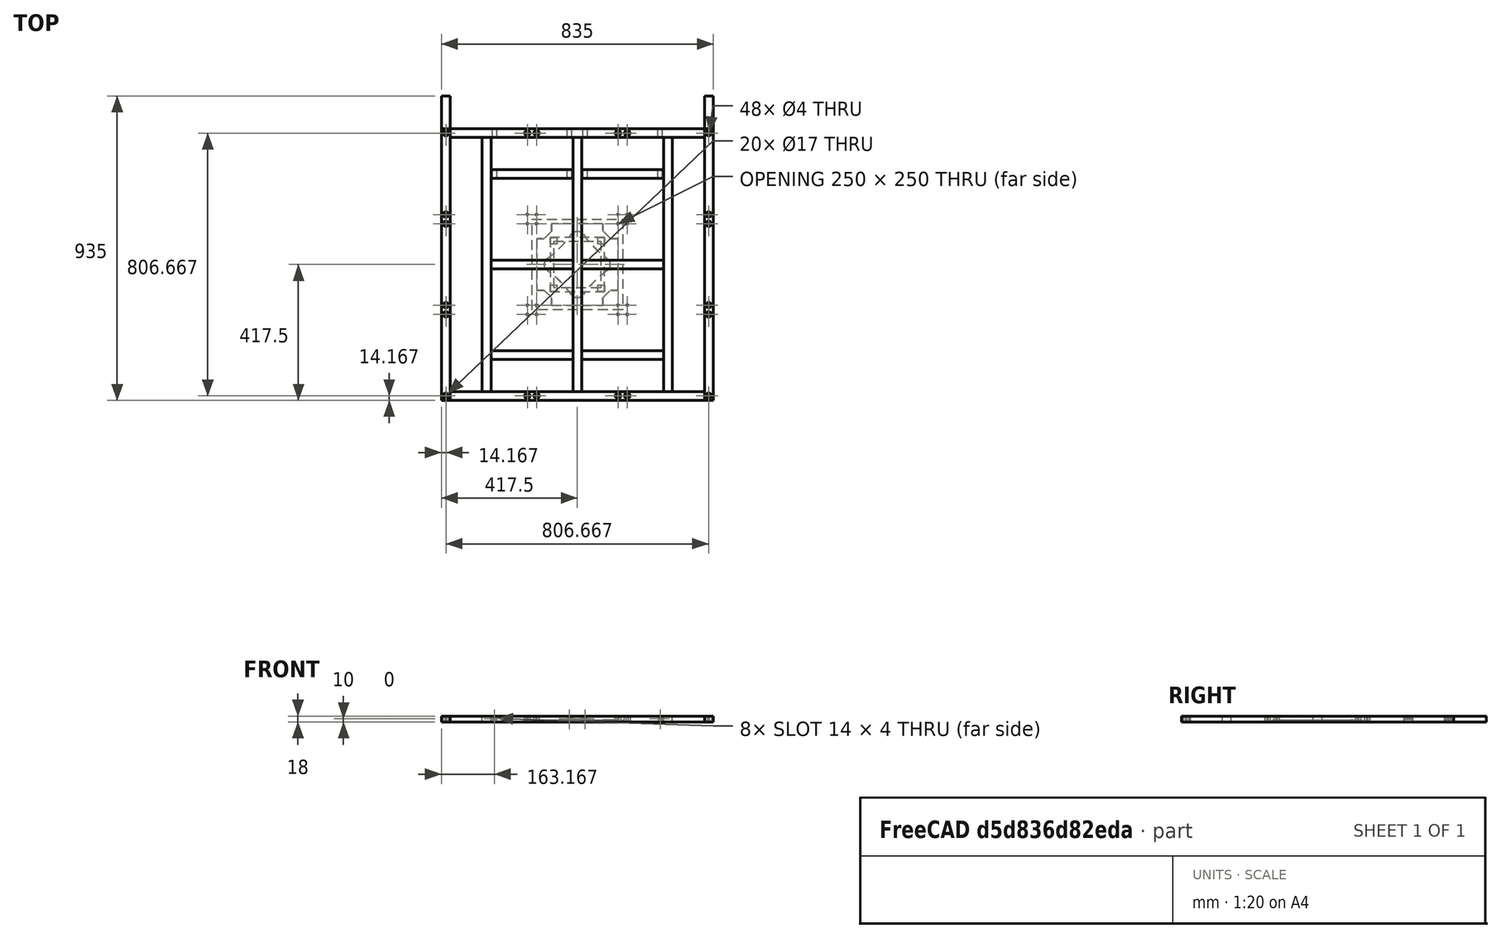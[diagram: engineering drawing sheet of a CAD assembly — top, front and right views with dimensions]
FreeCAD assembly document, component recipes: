
FREECAD ASSEMBLY — COMPONENT RECIPES ("DancePad")

This assembly document has 11 components, labeled P0..P10 below (a component is one placed body or linked part). 11 of them carry a construction recipe — the FreeCAD feature program that regenerates the part from scratch, quoted from this document or its linked companion documents; the rest are supplied as boundary geometry only. No exploded tour is included for this assembly.
COMPONENT P0 — recipe-attached ("Pad_UpLeft_Part - Link(Pad_Up_Part)", modeled in this document).
Construction recipe (the document's own serialized feature program — sketch geometry with constraints, then the solid features built on it; lengths are millimeters unless a unit is written):

FEATURE [Sketcher::SketchObject] Sketch002
  ArcFitTolerance = 0
  AttachmentSupport = -> [XY_Plane002]
  ExternalTypes = [0]
  FullyConstrained = true
  MakeInternals = false
  MapMode = 5
  _ExternalGeoVersion = 0
  expr: Constraints[10] = <<Variables>>.PadLength
  expr: Constraints[9] = <<Variables>>.PadLength
  sketch-geometry (4):
    g0: LineSegment StartX=-139 StartY=139 StartZ=0 EndX=139 EndY=139 EndZ=0
    g1: LineSegment StartX=139 StartY=139 StartZ=0 EndX=139 EndY=-139 EndZ=0
    g2: LineSegment StartX=139 StartY=-139 StartZ=0 EndX=-139 EndY=-139 EndZ=0
    g3: LineSegment StartX=-139 StartY=-139 StartZ=0 EndX=-139 EndY=139 EndZ=0
  constraints (11):
    c: Coincident(g0,g1)
    c: Coincident(g1,g2)
    c: Coincident(g2,g3)
    c: Coincident(g3,g0)
    c: Horizontal(g0)
    c: Horizontal(g2)
    c: Vertical(g1)
    c: Vertical(g3)
    c: Symmetric(g0,g1,g-1)
    c: DistanceX(g0,g0) = 278
    c: DistanceY(g1,g1) = 278
FEATURE [PartDesign::Pad] Pad002
  Direction = (0,0,1)
  Length = 6
  Length2 = 100
  Profile = -> Sketch002
  SideType = 0
  Suppressed = false
  Type = 0
  Type2 = 0
  expr: Length = <<Variables>>.PadThickness
FEATURE [Sketcher::SketchObject] Sketch003
  ArcFitTolerance = 0
  AttachmentSupport = -> [XY_Plane002]
  ExternalTypes = [0]
  FullyConstrained = true
  MakeInternals = false
  MapMode = 5
  _ExternalGeoVersion = 0
  expr: Constraints[22] = <<Variables>>.PadLength - 120
  expr: Constraints[24] = <<Variables>>.PadLength - 120
  expr: Constraints[28] = <<Variables>>.PadLength / 2 - 14
  expr: Constraints[29] = <<Variables>>.PadLength / 2 - 14
  sketch-geometry (16):
    g0: LineSegment StartX=-79 StartY=125 StartZ=0 EndX=79 EndY=125 EndZ=0
    g1: LineSegment StartX=79 StartY=125 StartZ=0 EndX=79 EndY=102 EndZ=0
    g2: LineSegment StartX=79 StartY=102 StartZ=0 EndX=102 EndY=79 EndZ=0
    g3: LineSegment StartX=102 StartY=79 StartZ=0 EndX=125 EndY=79 EndZ=0
    g4: LineSegment StartX=125 StartY=79 StartZ=0 EndX=125 EndY=-79 EndZ=0
    g5: LineSegment StartX=125 StartY=-79 StartZ=0 EndX=102 EndY=-79 EndZ=0
    g6: LineSegment StartX=102 StartY=-79 StartZ=0 EndX=79 EndY=-102 EndZ=0
    g7: LineSegment StartX=79 StartY=-102 StartZ=0 EndX=79 EndY=-125 EndZ=0
    g8: LineSegment StartX=79 StartY=-125 StartZ=0 EndX=-79 EndY=-125 EndZ=0
    g9: LineSegment StartX=-79 StartY=-125 StartZ=0 EndX=-79 EndY=-102 EndZ=0
    g10: LineSegment StartX=-79 StartY=-102 StartZ=0 EndX=-102 EndY=-79 EndZ=0
    g11: LineSegment StartX=-102 StartY=-79 StartZ=0 EndX=-125 EndY=-79 EndZ=0
    g12: LineSegment StartX=-125 StartY=-79 StartZ=0 EndX=-125 EndY=79 EndZ=0
    g13: LineSegment StartX=-125 StartY=79 StartZ=0 EndX=-102 EndY=79 EndZ=0
    g14: LineSegment StartX=-102 StartY=79 StartZ=0 EndX=-79 EndY=102 EndZ=0
    g15: LineSegment StartX=-79 StartY=102 StartZ=0 EndX=-79 EndY=125 EndZ=0
  constraints (38):
    c: Coincident(g0,g1)
    c: Vertical(g1)
    c: Coincident(g1,g2)
    c: Coincident(g2,g3)
    c: Horizontal(g3)
    c: Coincident(g3,g4)
    c: Vertical(g4)
    c: Coincident(g4,g5)
    c: Horizontal(g5)
    c: Coincident(g5,g6)
    c: Coincident(g6,g7)
    c: Vertical(g7)
    c: Coincident(g7,g8)
    c: Horizontal(g8)
    c: Coincident(g8,g9)
    c: Coincident(g9,g10)
    c: Coincident(g10,g11)
    c: Coincident(g11,g12)
    c: Coincident(g12,g13)
    c: Coincident(g13,g14)
    c: Coincident(g14,g15)
    c: Coincident(g15,g0)
    c: DistanceX(g0,g0) = 158
    c: Symmetric(g0,g0,g-2)
    c: DistanceY(g12,g12) = 158
    c: Symmetric(g12,g11,g-1)
    c: DistanceY(g15,g15) = 23
    c: DistanceX(g13,g13) = 23
    c: DistanceY(g-1,g0) = 125
    c: DistanceX(g12,g-1) = 125
    c: Symmetric(g14,g1,g-2)
    c: Symmetric(g13,g2,g-2)
    c: Symmetric(g12,g3,g-2)
    c: Symmetric(g13,g10,g-1)
    c: Symmetric(g14,g9,g-1)
    c: Symmetric(g0,g8,g-1)
    c: Symmetric(g13,g5,g-1)
    c: Symmetric(g14,g6,g-1)
FEATURE [PartDesign::Pocket] Pocket
  BaseFeature = -> Pad002
  Direction = (0,0,-1)
  Length = 5
  Length2 = 100
  Profile = -> Sketch003
  SideType = 2
  Suppressed = false
  Type = 1
  Type2 = 0
FEATURE [Sketcher::SketchObject] Sketch004  label="Sketch_Screw_Holes"
  ArcFitTolerance = 0
  AttachmentSupport = -> [Pad002]
  ExternalTypes = [0]
  FullyConstrained = true
  MakeInternals = false
  MapMode = 5
  Placement = pos=(0,0,0) rot=(1,0,0;3.14159rad)
  _ExternalGeoVersion = 0
  expr: Constraints[0] = <<Variables>>.PadScrewDiameter
  expr: Constraints[1] = <<Variables>>.PadScrewDiameter
  expr: Constraints[2] = <<Variables>>.PadScrewDiameter
  expr: Constraints[3] = <<Variables>>.PadScrewDiameter
  expr: Constraints[4] = <<Variables>>.PadLength / 2 - <<Variables>>.ScrewCornerPosition
  expr: Constraints[5] = <<Variables>>.PadLength / 2 - <<Variables>>.ScrewCornerPosition
  sketch-geometry (4):
    g0: Circle CenterX=-125 CenterY=125 CenterZ=0 NormalX=0 NormalY=0 NormalZ=1 AngleXU=0 Radius=2
    g1: Circle CenterX=125 CenterY=125 CenterZ=0 NormalX=0 NormalY=0 NormalZ=1 AngleXU=0 Radius=2
    g2: Circle CenterX=125 CenterY=-125 CenterZ=0 NormalX=0 NormalY=0 NormalZ=1 AngleXU=0 Radius=2
    g3: Circle CenterX=-125 CenterY=-125 CenterZ=0 NormalX=0 NormalY=0 NormalZ=1 AngleXU=0 Radius=2
  constraints (9):
    c: Diameter(g0) = 4
    c: Diameter(g1) = 4
    c: Diameter(g2) = 4
    c: Diameter(g3) = 4
    c: DistanceX(g0,g-1) = 125
    c: DistanceY(g-1,g0) = 125
    c: Symmetric(g0,g1,g-2)
    c: Symmetric(g0,g3,g-1)
    c: Symmetric(g0,g2,g-1)
FEATURE [PartDesign::Pocket] Pocket001  label="Screw_Pocket"
  BaseFeature = -> Pocket
  Direction = (0,0,1)
  Length = 5
  Length2 = 100
  Profile = -> Sketch004
  SideType = 2
  Suppressed = false
  Type = 1
  Type2 = 0
FEATURE [PartDesign::Fillet] Fillet
  Base = -> Pocket001 [Edge48,Edge40,Edge39,Edge47]
  BaseFeature = -> Pocket001
  Radius = 3
  SupportTransform = false
  Suppressed = false
  UseAllEdges = false
FEATURE [PartDesign::Body] Body002  label="Border_Body"
  AllowCompound = true
  Group = -> [Sketch002,Pad002,Sketch003,Sketch004,Pocket,Pocket001,Fillet]
  Origin = -> Origin008
  Tip = -> Fillet
COMPONENT P1 — same part as P0; its construction recipe is shown at P0.
COMPONENT P2 — same part as P0; its construction recipe is shown at P0.
COMPONENT P3 — same part as P0; its construction recipe is shown at P0.
COMPONENT P4 — same part as P0; its construction recipe is shown at P0.
COMPONENT P5 — same part as P0; its construction recipe is shown at P0.
COMPONENT P6 — same part as P0; its construction recipe is shown at P0.
COMPONENT P7 — recipe-attached ("PolycarbonatePad_Part", modeled in this document).
Construction recipe (the document's own serialized feature program — sketch geometry with constraints, then the solid features built on it; lengths are millimeters unless a unit is written):

FEATURE [Sketcher::SketchObject] Sketch022
  ArcFitTolerance = 0
  AttachmentSupport = -> [XY_Plane016]
  ExternalTypes = [0]
  FullyConstrained = true
  MakeInternals = false
  MapMode = 5
  _ExternalGeoVersion = 0
  expr: Constraints[8] = <<Variables>>.PadLength
  expr: Constraints[9] = <<Variables>>.PadLength
  sketch-geometry (4):
    g0: LineSegment StartX=-139 StartY=139 StartZ=0 EndX=139 EndY=139 EndZ=0
    g1: LineSegment StartX=139 StartY=139 StartZ=0 EndX=139 EndY=-139 EndZ=0
    g2: LineSegment StartX=139 StartY=-139 StartZ=0 EndX=-139 EndY=-139 EndZ=0
    g3: LineSegment StartX=-139 StartY=-139 StartZ=0 EndX=-139 EndY=139 EndZ=0
  constraints (11):
    c: Coincident(g0,g1)
    c: Coincident(g1,g2)
    c: Coincident(g2,g3)
    c: Coincident(g3,g0)
    c: Horizontal(g0)
    c: Horizontal(g2)
    c: Vertical(g1)
    c: Vertical(g3)
    c: DistanceX(g0,g0) = 278
    c: DistanceY(g1,g1) = 278
    c: Symmetric(g0,g1,g-1)
FEATURE [PartDesign::Pad] Pad015
  AlongSketchNormal = false
  Direction = (0,0,1)
  Length = 3
  Length2 = 100
  Profile = -> Sketch022
  SideType = 0
  Suppressed = false
  Type = 0
  Type2 = 0
  expr: Length = <<Variables>>.PolycarbonateThickness
FEATURE [Sketcher::SketchObject] Sketch023
  ArcFitTolerance = 0
  AttachmentSupport = -> [Pad015]
  ExternalTypes = [0]
  FullyConstrained = true
  MakeInternals = false
  MapMode = 5
  Placement = pos=(0,0,3) rot=(0,0,1;0rad)
  _ExternalGeoVersion = 0
  expr: Constraints[0] = <<Variables>>.PadScrewDiameter
  expr: Constraints[1] = <<Variables>>.PadScrewDiameter
  expr: Constraints[2] = <<Variables>>.PadScrewDiameter
  expr: Constraints[3] = <<Variables>>.PadScrewDiameter
  expr: Constraints[4] = <<Variables>>.PadLength / 2 - <<Variables>>.ScrewCornerPosition
  expr: Constraints[5] = <<Variables>>.PadLength / 2 - <<Variables>>.ScrewCornerPosition
  sketch-geometry (4):
    g0: Circle CenterX=-125 CenterY=125 CenterZ=0 NormalX=0 NormalY=0 NormalZ=1 AngleXU=0 Radius=2
    g1: Circle CenterX=125 CenterY=125 CenterZ=0 NormalX=0 NormalY=0 NormalZ=1 AngleXU=0 Radius=2
    g2: Circle CenterX=-125 CenterY=-125 CenterZ=0 NormalX=0 NormalY=0 NormalZ=1 AngleXU=0 Radius=2
    g3: Circle CenterX=125 CenterY=-125 CenterZ=0 NormalX=0 NormalY=0 NormalZ=1 AngleXU=0 Radius=2
  constraints (9):
    c: Diameter(g0) = 4
    c: Diameter(g1) = 4
    c: Diameter(g2) = 4
    c: Diameter(g3) = 4
    c: DistanceX(g0,g-1) = 125
    c: DistanceY(g-1,g0) = 125
    c: Symmetric(g0,g1,g-2)
    c: Symmetric(g0,g2,g-1)
    c: Symmetric(g0,g3,g-1)
FEATURE [PartDesign::Pocket] Pocket012
  BaseFeature = -> Pad015
  Direction = (0,0,-1)
  Length = 5
  Length2 = 100
  Profile = -> Sketch023
  SideType = 2
  Suppressed = false
  Type = 1
  Type2 = 0
FEATURE [PartDesign::Body] Body015
  AllowCompound = true
  Group = -> [Sketch022,Pad015,Sketch023,Pocket012]
  Origin = -> Origin027
  Tip = -> Pocket012
COMPONENT P8 — recipe-attached ("Body_Part", modeled in this document).
Construction recipe (the document's own serialized feature program — sketch geometry with constraints, then the solid features built on it; lengths are millimeters unless a unit is written):

FEATURE [Sketcher::SketchObject] Sketch
  ArcFitTolerance = 0
  AttachmentSupport = -> [XY_Plane]
  ExternalTypes = [0]
  FullyConstrained = true
  MakeInternals = false
  MapMode = 5
  _ExternalGeoVersion = 0
  expr: Constraints[10] = <<Variables>>.OveralPadLength
  expr: Constraints[9] = <<Variables>>.OveralPadLength
  sketch-geometry (4):
    g0: LineSegment StartX=-417.5 StartY=417.5 StartZ=0 EndX=417.5 EndY=417.5 EndZ=0
    g1: LineSegment StartX=417.5 StartY=417.5 StartZ=0 EndX=417.5 EndY=-417.5 EndZ=0
    g2: LineSegment StartX=417.5 StartY=-417.5 StartZ=0 EndX=-417.5 EndY=-417.5 EndZ=0
    g3: LineSegment StartX=-417.5 StartY=-417.5 StartZ=0 EndX=-417.5 EndY=417.5 EndZ=0
  constraints (11):
    c: Coincident(g0,g1)
    c: Coincident(g1,g2)
    c: Coincident(g2,g3)
    c: Coincident(g3,g0)
    c: Horizontal(g0)
    c: Horizontal(g2)
    c: Vertical(g1)
    c: Vertical(g3)
    c: Symmetric(g0,g1,g-1)
    c: DistanceX(g0,g0) = 835
    c: DistanceY(g1,g1) = 835
FEATURE [PartDesign::Pad] Pad
  Direction = (0,0,1)
  Length = 18
  Length2 = 100
  Profile = -> Sketch
  SideType = 0
  Suppressed = false
  Type = 0
  Type2 = 0
  expr: Length = <<Variables>>.OverallPadThickness
FEATURE [PartDesign::SubShapeBinder] Binder  label="Binder(Sketch_Screw_Holes)"
  BindCopyOnChange = 0
  BindMode = 0
  ClaimChildren = false
  Context = -> Part001 [Body.Binder.]
  Fuse = false
  MakeFace = true
  OffsetFill = false
  OffsetIntersection = false
  OffsetJoinType = 0
  OffsetOpenResult = false
  PartialLoad = false
  Relative = true
  Support = -> [Part002[Body002.Sketch004.]]
  _Version = 8
FEATURE [PartDesign::SubShapeBinder] Binder001  label="Binder001(Sketch_Screw_Holes)"
  BindCopyOnChange = 0
  BindMode = 0
  ClaimChildren = false
  Context = -> Part001 [Body.Binder001.]
  Fuse = false
  MakeFace = true
  OffsetFill = false
  OffsetIntersection = false
  OffsetJoinType = 0
  OffsetOpenResult = false
  PartialLoad = false
  Relative = true
  Support = -> [Link[Body002.Sketch004.]]
  _Version = 8
FEATURE [PartDesign::SubShapeBinder] Binder002  label="Binder002(Sketch_Screw_Holes)"
  BindCopyOnChange = 0
  BindMode = 0
  ClaimChildren = false
  Context = -> Part001 [Body.Binder002.]
  Fuse = false
  MakeFace = true
  OffsetFill = false
  OffsetIntersection = false
  OffsetJoinType = 0
  OffsetOpenResult = false
  PartialLoad = false
  Relative = true
  Support = -> [Link015[Body002.Sketch004.]]
  _Version = 8
FEATURE [PartDesign::SubShapeBinder] Binder003  label="Binder003(Sketch_Screw_Holes)"
  BindCopyOnChange = 0
  BindMode = 0
  ClaimChildren = false
  Context = -> Part001 [Body.Binder003.]
  Fuse = false
  MakeFace = true
  OffsetFill = false
  OffsetIntersection = false
  OffsetJoinType = 0
  OffsetOpenResult = false
  PartialLoad = false
  Relative = true
  Support = -> [Link016[Body002.Sketch004.]]
  _Version = 8
FEATURE [PartDesign::SubShapeBinder] Binder004  label="Binder004(Sketch_Screw_Holes)"
  BindCopyOnChange = 0
  BindMode = 0
  ClaimChildren = false
  Context = -> Part001 [Body.Binder004.]
  Fuse = false
  MakeFace = true
  OffsetFill = false
  OffsetIntersection = false
  OffsetJoinType = 0
  OffsetOpenResult = false
  PartialLoad = false
  Relative = true
  Support = -> [Link017[Body002.Sketch004.]]
  _Version = 8
FEATURE [PartDesign::SubShapeBinder] Binder005  label="Binder005(Sketch_Screw_Holes)"
  BindCopyOnChange = 0
  BindMode = 0
  ClaimChildren = false
  Context = -> Part001 [Body.Binder005.]
  Fuse = false
  MakeFace = true
  OffsetFill = false
  OffsetIntersection = false
  OffsetJoinType = 0
  OffsetOpenResult = false
  PartialLoad = false
  Relative = true
  Support = -> [Link018[Body002.Sketch004.]]
  _Version = 8
FEATURE [PartDesign::SubShapeBinder] Binder006  label="Binder006(Sketch_Screw_Holes)"
  BindCopyOnChange = 0
  BindMode = 0
  ClaimChildren = false
  Context = -> Part001 [Body.Binder006.]
  Fuse = false
  MakeFace = true
  OffsetFill = false
  OffsetIntersection = false
  OffsetJoinType = 0
  OffsetOpenResult = false
  PartialLoad = false
  Relative = true
  Support = -> [Link019[Body002.Sketch004.]]
  _Version = 8
FEATURE [PartDesign::SubShapeBinder] Binder007  label="Binder007(Sketch_Screw_Holes)"
  BindCopyOnChange = 0
  BindMode = 0
  ClaimChildren = false
  Context = -> Part001 [Body.Binder007.]
  Fuse = false
  MakeFace = true
  OffsetFill = false
  OffsetIntersection = false
  OffsetJoinType = 0
  OffsetOpenResult = false
  PartialLoad = false
  Relative = true
  Support = -> [Link020[Body002.Sketch004.]]
  _Version = 8
FEATURE [PartDesign::SubShapeBinder] Binder008  label="Binder008(Sketch021)"
  BindCopyOnChange = 0
  BindMode = 0
  ClaimChildren = false
  Context = -> Part001 [Body.Binder008.]
  Fuse = false
  MakeFace = true
  OffsetFill = false
  OffsetIntersection = false
  OffsetJoinType = 0
  OffsetOpenResult = false
  PartialLoad = false
  Relative = true
  Support = -> [Part007[Body014.Sketch021.]]
  _Version = 8
FEATURE [Sketcher::SketchObject] Sketch028
  ArcFitTolerance = 0
  AttachmentSupport = -> [Pad]
  ExternalGeometry = -> [Binder001,Binder,Binder002,Binder003,Binder008,Binder004,Binder005,Binder007,Binder006]
  ExternalTypes = [0]
  FullyConstrained = true
  MakeInternals = false
  MapMode = 5
  Placement = pos=(0,0,18) rot=(0,0,1;0rad)
  _ExternalGeoVersion = 0
  expr: Constraints[36] = <<Variables>>.PadScrewDiameter
  expr: Constraints[37] = <<Variables>>.PadScrewDiameter
  expr: Constraints[38] = <<Variables>>.PadScrewDiameter
  expr: Constraints[39] = <<Variables>>.PadScrewDiameter
  expr: Constraints[40] = <<Variables>>.PadScrewDiameter
  expr: Constraints[41] = <<Variables>>.PadScrewDiameter
  expr: Constraints[42] = <<Variables>>.PadScrewDiameter
  expr: Constraints[43] = <<Variables>>.PadScrewDiameter
  expr: Constraints[44] = <<Variables>>.PadScrewDiameter
  expr: Constraints[45] = <<Variables>>.PadScrewDiameter
  expr: Constraints[46] = <<Variables>>.PadScrewDiameter
  expr: Constraints[47] = <<Variables>>.PadScrewDiameter
  expr: Constraints[48] = <<Variables>>.PadScrewDiameter
  expr: Constraints[49] = <<Variables>>.PadScrewDiameter
  expr: Constraints[50] = <<Variables>>.PadScrewDiameter
  expr: Constraints[51] = <<Variables>>.PadScrewDiameter
  expr: Constraints[52] = <<Variables>>.PadScrewDiameter
  expr: Constraints[53] = <<Variables>>.PadScrewDiameter
  expr: Constraints[54] = <<Variables>>.PadScrewDiameter
  expr: Constraints[55] = <<Variables>>.PadScrewDiameter
  expr: Constraints[56] = <<Variables>>.PadScrewDiameter
  expr: Constraints[57] = <<Variables>>.PadScrewDiameter
  expr: Constraints[58] = <<Variables>>.PadScrewDiameter
  expr: Constraints[59] = <<Variables>>.PadScrewDiameter
  expr: Constraints[60] = <<Variables>>.PadScrewDiameter
  expr: Constraints[61] = <<Variables>>.PadScrewDiameter
  expr: Constraints[62] = <<Variables>>.PadScrewDiameter
  expr: Constraints[63] = <<Variables>>.PadScrewDiameter
  expr: Constraints[64] = <<Variables>>.PadScrewDiameter
  expr: Constraints[65] = <<Variables>>.PadScrewDiameter
  expr: Constraints[66] = <<Variables>>.PadScrewDiameter
  expr: Constraints[67] = <<Variables>>.PadScrewDiameter
  expr: Constraints[68] = <<Variables>>.PadScrewDiameter
  expr: Constraints[69] = <<Variables>>.PadScrewDiameter
  expr: Constraints[70] = <<Variables>>.PadScrewDiameter
  expr: Constraints[71] = <<Variables>>.PadScrewDiameter
  sketch-geometry (36):
    g0: Circle CenterX=-403.333 CenterY=403.333 CenterZ=0 NormalX=0 NormalY=0 NormalZ=1 AngleXU=0 Radius=2
    g1: Circle CenterX=-153.333 CenterY=403.333 CenterZ=0 NormalX=0 NormalY=0 NormalZ=1 AngleXU=0 Radius=2
    g2: Circle CenterX=-125 CenterY=403.333 CenterZ=0 NormalX=0 NormalY=0 NormalZ=1 AngleXU=0 Radius=2
    g3: Circle CenterX=125 CenterY=403.333 CenterZ=0 NormalX=0 NormalY=0 NormalZ=1 AngleXU=0 Radius=2
    g4: Circle CenterX=153.333 CenterY=403.333 CenterZ=0 NormalX=0 NormalY=0 NormalZ=1 AngleXU=0 Radius=2
    g5: Circle CenterX=403.333 CenterY=403.333 CenterZ=0 NormalX=0 NormalY=0 NormalZ=1 AngleXU=0 Radius=2
    g6: Circle CenterX=-403.333 CenterY=153.333 CenterZ=0 NormalX=0 NormalY=0 NormalZ=1 AngleXU=0 Radius=2
    g7: Circle CenterX=-153.333 CenterY=153.333 CenterZ=0 NormalX=0 NormalY=0 NormalZ=1 AngleXU=0 Radius=2
    g8: Circle CenterX=-125 CenterY=153.333 CenterZ=0 NormalX=0 NormalY=0 NormalZ=1 AngleXU=0 Radius=2
    g9: Circle CenterX=125 CenterY=153.333 CenterZ=0 NormalX=0 NormalY=0 NormalZ=1 AngleXU=0 Radius=2
    g10: Circle CenterX=153.333 CenterY=153.333 CenterZ=0 NormalX=0 NormalY=0 NormalZ=1 AngleXU=0 Radius=2
    g11: Circle CenterX=403.333 CenterY=153.333 CenterZ=0 NormalX=0 NormalY=0 NormalZ=1 AngleXU=0 Radius=2
    g12: Circle CenterX=-403.333 CenterY=125 CenterZ=0 NormalX=0 NormalY=0 NormalZ=1 AngleXU=0 Radius=2
    g13: Circle CenterX=-153.333 CenterY=125 CenterZ=0 NormalX=0 NormalY=0 NormalZ=1 AngleXU=0 Radius=2
    g14: Circle CenterX=-125 CenterY=125 CenterZ=0 NormalX=0 NormalY=0 NormalZ=1 AngleXU=0 Radius=2
    g15: Circle CenterX=125 CenterY=125 CenterZ=0 NormalX=0 NormalY=0 NormalZ=1 AngleXU=0 Radius=2
    g16: Circle CenterX=153.333 CenterY=125 CenterZ=0 NormalX=0 NormalY=0 NormalZ=1 AngleXU=0 Radius=2
    g17: Circle CenterX=403.333 CenterY=125 CenterZ=0 NormalX=0 NormalY=0 NormalZ=1 AngleXU=0 Radius=2
    g18: Circle CenterX=-403.333 CenterY=-125 CenterZ=0 NormalX=0 NormalY=0 NormalZ=1 AngleXU=0 Radius=2
    g19: Circle CenterX=-153.333 CenterY=-125 CenterZ=0 NormalX=0 NormalY=0 NormalZ=1 AngleXU=0 Radius=2
    g20: Circle CenterX=-125 CenterY=-125 CenterZ=0 NormalX=0 NormalY=0 NormalZ=1 AngleXU=0 Radius=2
    g21: Circle CenterX=125 CenterY=-125 CenterZ=0 NormalX=0 NormalY=0 NormalZ=1 AngleXU=0 Radius=2
    g22: Circle CenterX=153.333 CenterY=-125 CenterZ=0 NormalX=0 NormalY=0 NormalZ=1 AngleXU=0 Radius=2
    g23: Circle CenterX=403.333 CenterY=-125 CenterZ=0 NormalX=0 NormalY=0 NormalZ=1 AngleXU=0 Radius=2
    g24: Circle CenterX=-403.333 CenterY=-153.333 CenterZ=0 NormalX=0 NormalY=0 NormalZ=1 AngleXU=0 Radius=2
    g25: Circle CenterX=-153.333 CenterY=-153.333 CenterZ=0 NormalX=0 NormalY=0 NormalZ=1 AngleXU=0 Radius=2
    g26: Circle CenterX=-125 CenterY=-153.333 CenterZ=0 NormalX=0 NormalY=0 NormalZ=1 AngleXU=0 Radius=2
    g27: Circle CenterX=125 CenterY=-153.333 CenterZ=0 NormalX=0 NormalY=0 NormalZ=1 AngleXU=0 Radius=2
    g28: Circle CenterX=153.333 CenterY=-153.333 CenterZ=0 NormalX=0 NormalY=0 NormalZ=1 AngleXU=0 Radius=2
    g29: Circle CenterX=403.333 CenterY=-153.333 CenterZ=0 NormalX=0 NormalY=0 NormalZ=1 AngleXU=0 Radius=2
    g30: Circle CenterX=-403.333 CenterY=-403.333 CenterZ=0 NormalX=0 NormalY=0 NormalZ=1 AngleXU=0 Radius=2
    g31: Circle CenterX=-153.333 CenterY=-403.333 CenterZ=0 NormalX=0 NormalY=0 NormalZ=1 AngleXU=0 Radius=2
    g32: Circle CenterX=-125 CenterY=-403.333 CenterZ=0 NormalX=0 NormalY=0 NormalZ=1 AngleXU=0 Radius=2
    g33: Circle CenterX=125 CenterY=-403.333 CenterZ=0 NormalX=0 NormalY=0 NormalZ=1 AngleXU=0 Radius=2
    g34: Circle CenterX=153.333 CenterY=-403.333 CenterZ=0 NormalX=0 NormalY=0 NormalZ=1 AngleXU=0 Radius=2
    g35: Circle CenterX=403.333 CenterY=-403.333 CenterZ=0 NormalX=0 NormalY=0 NormalZ=1 AngleXU=0 Radius=2
  constraints (72):
    c: Coincident(g0,g-3)
    c: Coincident(g1,g-4)
    c: Coincident(g2,g-5)
    c: Coincident(g3,g-6)
    c: Coincident(g4,g-7)
    c: Coincident(g5,g-8)
    c: Coincident(g6,g-9)
    c: Coincident(g7,g-10)
    c: Coincident(g8,g-11)
    c: Coincident(g9,g-12)
    c: Coincident(g10,g-13)
    c: Coincident(g11,g-14)
    c: Coincident(g12,g-15)
    c: Coincident(g13,g-16)
    c: Coincident(g14,g-17)
    c: Coincident(g15,g-18)
    c: Coincident(g16,g-19)
    c: Coincident(g17,g-20)
    c: Coincident(g18,g-21)
    c: Coincident(g19,g-22)
    c: Coincident(g20,g-23)
    c: Coincident(g21,g-24)
    c: Coincident(g22,g-25)
    c: Coincident(g23,g-26)
    c: Coincident(g24,g-27)
    c: Coincident(g25,g-28)
    c: Coincident(g26,g-29)
    c: Coincident(g27,g-30)
    c: Coincident(g28,g-31)
    c: Coincident(g29,g-32)
    c: Coincident(g30,g-33)
    c: Coincident(g31,g-34)
    c: Coincident(g32,g-35)
    c: Coincident(g33,g-36)
    c: Coincident(g34,g-37)
    c: Coincident(g35,g-38)
    c: Diameter(g0) = 4
    c: Diameter(g1) = 4
    c: Diameter(g2) = 4
    c: Diameter(g3) = 4
    c: Diameter(g4) = 4
    c: Diameter(g5) = 4
    c: Diameter(g6) = 4
    c: Diameter(g7) = 4
    c: Diameter(g8) = 4
    c: Diameter(g9) = 4
    c: Diameter(g10) = 4
    c: Diameter(g11) = 4
    c: Diameter(g12) = 4
    c: Diameter(g13) = 4
    c: Diameter(g14) = 4
    c: Diameter(g15) = 4
    c: Diameter(g16) = 4
    c: Diameter(g17) = 4
    c: Diameter(g18) = 4
    c: Diameter(g19) = 4
    c: Diameter(g20) = 4
    c: Diameter(g21) = 4
    c: Diameter(g22) = 4
    c: Diameter(g23) = 4
    c: Diameter(g24) = 4
    c: Diameter(g25) = 4
    c: Diameter(g26) = 4
    c: Diameter(g27) = 4
    c: Diameter(g28) = 4
    c: Diameter(g29) = 4
    c: Diameter(g30) = 4
    c: Diameter(g31) = 4
    c: Diameter(g32) = 4
    c: Diameter(g33) = 4
    c: Diameter(g34) = 4
    c: Diameter(g35) = 4
FEATURE [PartDesign::Pocket] Pocket013
  BaseFeature = -> Pad
  Direction = (0,0,-1)
  Length = 5
  Length2 = 100
  Profile = -> Sketch028
  SideType = 2
  Suppressed = false
  Type = 1
  Type2 = 0
FEATURE [PartDesign::Body] Body
  AllowCompound = true
  Group = -> [Sketch,Pad,Binder,Binder001,Binder002,Binder003,Binder004,Binder005,Binder006,Binder007,Binder008,Sketch028,Pocket013]
  Origin = -> Origin
  Tip = -> Pocket013
COMPONENT P9 — recipe-attached ("Pad_Middle_Part", modeled in this document).
Construction recipe (the document's own serialized feature program — sketch geometry with constraints, then the solid features built on it; lengths are millimeters unless a unit is written):

FEATURE [Sketcher::SketchObject] Sketch020
  ArcFitTolerance = 0
  AttachmentSupport = -> [XY_Plane015]
  ExternalTypes = [0]
  FullyConstrained = true
  MakeInternals = false
  MapMode = 5
  _ExternalGeoVersion = 0
  expr: Constraints[8] = <<Variables>>.PadLength
  expr: Constraints[9] = <<Variables>>.PadLength
  sketch-geometry (4):
    g0: LineSegment StartX=-139 StartY=139 StartZ=0 EndX=139 EndY=139 EndZ=0
    g1: LineSegment StartX=139 StartY=139 StartZ=0 EndX=139 EndY=-139 EndZ=0
    g2: LineSegment StartX=139 StartY=-139 StartZ=0 EndX=-139 EndY=-139 EndZ=0
    g3: LineSegment StartX=-139 StartY=-139 StartZ=0 EndX=-139 EndY=139 EndZ=0
  constraints (11):
    c: Coincident(g0,g1)
    c: Coincident(g1,g2)
    c: Coincident(g2,g3)
    c: Coincident(g3,g0)
    c: Horizontal(g0)
    c: Horizontal(g2)
    c: Vertical(g1)
    c: Vertical(g3)
    c: DistanceX(g0,g0) = 278
    c: DistanceY(g1,g1) = 278
    c: Symmetric(g0,g1,g-1)
FEATURE [PartDesign::Pad] Pad014
  AlongSketchNormal = false
  Direction = (0,0,1)
  Length = 6
  Length2 = 100
  Profile = -> Sketch020
  SideType = 0
  Suppressed = false
  Type = 0
  Type2 = 0
  expr: Length = <<Variables>>.PadThickness
FEATURE [Sketcher::SketchObject] Sketch021
  ArcFitTolerance = 0
  AttachmentSupport = -> [Pad014]
  ExternalTypes = [0]
  FullyConstrained = true
  MakeInternals = false
  MapMode = 5
  Placement = pos=(0,0,6) rot=(0,0,1;0rad)
  _ExternalGeoVersion = 0
  expr: Constraints[0] = <<Variables>>.PadScrewDiameter
  expr: Constraints[1] = <<Variables>>.PadScrewDiameter
  expr: Constraints[2] = <<Variables>>.PadScrewDiameter
  expr: Constraints[3] = <<Variables>>.PadScrewDiameter
  expr: Constraints[4] = <<Variables>>.PadLength / 2 - <<Variables>>.ScrewCornerPosition
  expr: Constraints[5] = <<Variables>>.PadLength / 2 - <<Variables>>.ScrewCornerPosition
  sketch-geometry (4):
    g0: Circle CenterX=-125 CenterY=125 CenterZ=0 NormalX=0 NormalY=0 NormalZ=1 AngleXU=0 Radius=2
    g1: Circle CenterX=125 CenterY=125 CenterZ=0 NormalX=0 NormalY=0 NormalZ=1 AngleXU=0 Radius=2
    g2: Circle CenterX=-125 CenterY=-125 CenterZ=0 NormalX=0 NormalY=0 NormalZ=1 AngleXU=0 Radius=2
    g3: Circle CenterX=125 CenterY=-125 CenterZ=0 NormalX=0 NormalY=0 NormalZ=1 AngleXU=0 Radius=2
  constraints (9):
    c: Diameter(g0) = 4
    c: Diameter(g1) = 4
    c: Diameter(g2) = 4
    c: Diameter(g3) = 4
    c: DistanceX(g0,g-1) = 125
    c: DistanceY(g-1,g0) = 125
    c: Symmetric(g0,g1,g-2)
    c: Symmetric(g0,g2,g-1)
    c: Symmetric(g0,g3,g-1)
FEATURE [PartDesign::Pocket] Pocket011  label="ScrewMidde_Pocket"
  BaseFeature = -> Pad014
  Direction = (0,0,-1)
  Length = 5
  Length2 = 100
  Profile = -> Sketch021
  SideType = 2
  Suppressed = false
  Type = 1
  Type2 = 0
FEATURE [PartDesign::Body] Body014
  AllowCompound = true
  Group = -> [Sketch020,Pad014,Sketch021,Pocket011]
  Origin = -> Origin025
  Tip = -> Pocket011
COMPONENT P10 — recipe-attached ("Supports_Part", modeled in this document).
Construction recipe (the document's own serialized feature program — sketch geometry with constraints, then the solid features built on it; lengths are millimeters unless a unit is written):

FEATURE [Sketcher::SketchObject] Sketch029
  ArcFitTolerance = 0
  AttachmentSupport = -> [XY_Plane021]
  ExternalTypes = [0]
  FullyConstrained = true
  MakeInternals = false
  MapMode = 5
  _ExternalGeoVersion = 0
  expr: Constraints[8] = <<Variables>>.SupportHeight
  expr: Constraints[9] = <<Variables>>.OveralPadLength + <<Variables>>.CommandWidth
  sketch-geometry (4):
    g0: LineSegment StartX=-13.5 StartY=467.5 StartZ=0 EndX=13.5 EndY=467.5 EndZ=0
    g1: LineSegment StartX=13.5 StartY=467.5 StartZ=0 EndX=13.5 EndY=-467.5 EndZ=0
    g2: LineSegment StartX=13.5 StartY=-467.5 StartZ=0 EndX=-13.5 EndY=-467.5 EndZ=0
    g3: LineSegment StartX=-13.5 StartY=-467.5 StartZ=0 EndX=-13.5 EndY=467.5 EndZ=0
  constraints (11):
    c: Coincident(g0,g1)
    c: Coincident(g1,g2)
    c: Coincident(g2,g3)
    c: Coincident(g3,g0)
    c: Horizontal(g0)
    c: Horizontal(g2)
    c: Vertical(g1)
    c: Vertical(g3)
    c: DistanceX(g0,g0) = 27
    c: DistanceY(g3,g3) = 935
    c: Symmetric(g0,g1,g-1)
FEATURE [PartDesign::Pad] Pad020
  AlongSketchNormal = false
  Direction = (0,0,1)
  Length = 18
  Length2 = 100
  Profile = -> Sketch029
  SideType = 0
  Suppressed = false
  Type = 0
  Type2 = 0
FEATURE [Sketcher::SketchObject] Sketch030
  ArcFitTolerance = 0
  AttachmentSupport = -> [XY_Plane022]
  ExternalTypes = [0]
  FullyConstrained = true
  MakeInternals = false
  MapMode = 5
  _ExternalGeoVersion = 0
  expr: Constraints[10] = <<Variables>>.SupportHeight
  expr: Constraints[9] = <<Variables>>.OveralPadLength - 2 * <<Variables>>.SupportHeight
  sketch-geometry (4):
    g0: LineSegment StartX=-390.5 StartY=13.5 StartZ=0 EndX=390.5 EndY=13.5 EndZ=0
    g1: LineSegment StartX=390.5 StartY=13.5 StartZ=0 EndX=390.5 EndY=-13.5 EndZ=0
    g2: LineSegment StartX=390.5 StartY=-13.5 StartZ=0 EndX=-390.5 EndY=-13.5 EndZ=0
    g3: LineSegment StartX=-390.5 StartY=-13.5 StartZ=0 EndX=-390.5 EndY=13.5 EndZ=0
  constraints (11):
    c: Coincident(g0,g1)
    c: Coincident(g1,g2)
    c: Coincident(g2,g3)
    c: Coincident(g3,g0)
    c: Horizontal(g0)
    c: Horizontal(g2)
    c: Vertical(g1)
    c: Vertical(g3)
    c: Symmetric(g0,g1,g-1)
    c: DistanceX(g0,g0) = 781
    c: DistanceY(g1,g1) = 27
FEATURE [PartDesign::Pad] Pad021
  AlongSketchNormal = false
  Direction = (0,0,1)
  Length = 18
  Length2 = 100
  Profile = -> Sketch030
  SideType = 0
  Suppressed = false
  Type = 0
  Type2 = 0
  expr: Length = <<Variables>>.SupportThickness
FEATURE [Sketcher::SketchObject] Sketch031
  ArcFitTolerance = 0
  AttachmentSupport = -> [XY_Plane023]
  ExternalTypes = [0]
  FullyConstrained = true
  MakeInternals = false
  MapMode = 5
  _ExternalGeoVersion = 0
  expr: Constraints[10] = <<Variables>>.SupportHeight
  expr: Constraints[9] = <<Variables>>.OveralPadLength - 2 * <<Variables>>.SupportHeight
  sketch-geometry (4):
    g0: LineSegment StartX=-390.5 StartY=13.5 StartZ=0 EndX=390.5 EndY=13.5 EndZ=0
    g1: LineSegment StartX=390.5 StartY=13.5 StartZ=0 EndX=390.5 EndY=-13.5 EndZ=0
    g2: LineSegment StartX=390.5 StartY=-13.5 StartZ=0 EndX=-390.5 EndY=-13.5 EndZ=0
    g3: LineSegment StartX=-390.5 StartY=-13.5 StartZ=0 EndX=-390.5 EndY=13.5 EndZ=0
  constraints (11):
    c: Coincident(g0,g1)
    c: Coincident(g1,g2)
    c: Coincident(g2,g3)
    c: Coincident(g3,g0)
    c: Horizontal(g0)
    c: Horizontal(g2)
    c: Vertical(g1)
    c: Vertical(g3)
    c: Symmetric(g0,g1,g-1)
    c: DistanceX(g0,g0) = 781
    c: DistanceY(g1,g1) = 27
FEATURE [PartDesign::Pad] Pad022
  AlongSketchNormal = false
  Direction = (0,0,1)
  Length = 18
  Length2 = 100
  Profile = -> Sketch031
  SideType = 0
  Suppressed = false
  Type = 0
  Type2 = 0
  expr: Length = <<Variables>>.SupportThickness
FEATURE [Sketcher::SketchObject] Sketch032
  ArcFitTolerance = 0
  AttachmentSupport = -> [XY_Plane024]
  ExternalTypes = [0]
  FullyConstrained = true
  MakeInternals = false
  MapMode = 5
  _ExternalGeoVersion = 0
  expr: Constraints[8] = <<Variables>>.SupportHeight
  expr: Constraints[9] = <<Variables>>.OveralPadLength - 2 * <<Variables>>.SupportHeight
  sketch-geometry (4):
    g0: LineSegment StartX=-13.5 StartY=390.5 StartZ=0 EndX=13.5 EndY=390.5 EndZ=0
    g1: LineSegment StartX=13.5 StartY=390.5 StartZ=0 EndX=13.5 EndY=-390.5 EndZ=0
    g2: LineSegment StartX=13.5 StartY=-390.5 StartZ=0 EndX=-13.5 EndY=-390.5 EndZ=0
    g3: LineSegment StartX=-13.5 StartY=-390.5 StartZ=0 EndX=-13.5 EndY=390.5 EndZ=0
  constraints (11):
    c: Coincident(g0,g1)
    c: Coincident(g1,g2)
    c: Coincident(g2,g3)
    c: Coincident(g3,g0)
    c: Horizontal(g0)
    c: Horizontal(g2)
    c: Vertical(g1)
    c: Vertical(g3)
    c: DistanceX(g0,g0) = 27
    c: DistanceY(g1,g1) = 781
    c: Symmetric(g0,g1,g-1)
FEATURE [PartDesign::Pad] Pad023
  AlongSketchNormal = false
  Direction = (0,0,1)
  Length = 18
  Length2 = 100
  Profile = -> Sketch032
  SideType = 0
  Suppressed = false
  Type = 0
  Type2 = 0
  expr: Length = <<Variables>>.SupportThickness
FEATURE [PartDesign::LinearPattern] LinearPattern006
  BaseFeature = -> Pad023
  Direction = -> X_Axis024
  Length = 556.667
  Length2 = 100
  Mode = 0
  Mode2 = 0
  Occurrences = 3
  Occurrences2 = 1
  Offset = 278.333
  Offset2 = 10
  Reversed2 = false
  SpacingPattern = [0]
  SpacingPattern2 = [0]
  Spacings = [-1,-1]
  Spacings2 = [0]
  Suppressed = false
  TransformMode = 0
  expr: Length = <<Variables>>.OveralPadLength / 3 * 2
FEATURE [PartDesign::Body] Body023  label="VerticalCrossing_Body"
  AllowCompound = true
  Group = -> [Sketch032,Pad023,LinearPattern006]
  Origin = -> Origin038
  Placement = pos=(-278.333,0,0) rot=(0,0,1;0rad)
  Tip = -> LinearPattern006
  expr: .Placement.Base.x = -(<<Variables>>.OveralPadLength / 3)
FEATURE [Sketcher::SketchObject] Sketch033
  ArcFitTolerance = 0
  AttachmentSupport = -> [Pad022]
  ExternalTypes = [0]
  FullyConstrained = true
  MakeInternals = false
  MapMode = 5
  Placement = pos=(0,13.5,0) rot=(0,0.707107,0.707107;3.14159rad)
  _ExternalGeoVersion = 0
  sketch-geometry (16):
    g0: ArcOfCircle CenterX=-259.333 CenterY=10 CenterZ=0 NormalX=0 NormalY=0 NormalZ=1 AngleXU=0 Radius=2 StartAngle=1.5708 EndAngle=4.71239
    g1: ArcOfCircle CenterX=-249.333 CenterY=10 CenterZ=0 NormalX=0 NormalY=0 NormalZ=1 AngleXU=0 Radius=2 StartAngle=4.71239 EndAngle=7.85398
    g2: LineSegment StartX=-259.333 StartY=8 StartZ=0 EndX=-249.333 EndY=8 EndZ=0
    g3: LineSegment StartX=-249.333 StartY=12 StartZ=0 EndX=-259.333 EndY=12 EndZ=0
    g4: ArcOfCircle CenterX=-29.3333 CenterY=10 CenterZ=0 NormalX=0 NormalY=0 NormalZ=1 AngleXU=0 Radius=2 StartAngle=1.5708 EndAngle=4.71239
    g5: ArcOfCircle CenterX=-19.3333 CenterY=10 CenterZ=0 NormalX=0 NormalY=0 NormalZ=1 AngleXU=0 Radius=2 StartAngle=4.71239 EndAngle=7.85398
    g6: LineSegment StartX=-29.3333 StartY=8 StartZ=0 EndX=-19.3333 EndY=8 EndZ=0
    g7: LineSegment StartX=-19.3333 StartY=12 StartZ=0 EndX=-29.3333 EndY=12 EndZ=0
    g8: ArcOfCircle CenterX=19.3333 CenterY=10 CenterZ=0 NormalX=0 NormalY=0 NormalZ=1 AngleXU=0 Radius=2 StartAngle=1.5708 EndAngle=4.71239
    g9: ArcOfCircle CenterX=29.3333 CenterY=10 CenterZ=0 NormalX=0 NormalY=0 NormalZ=1 AngleXU=0 Radius=2 StartAngle=4.71239 EndAngle=7.85398
    g10: LineSegment StartX=19.3333 StartY=8 StartZ=0 EndX=29.3333 EndY=8 EndZ=0
    g11: LineSegment StartX=29.3333 StartY=12 StartZ=0 EndX=19.3333 EndY=12 EndZ=0
    g12: ArcOfCircle CenterX=249.333 CenterY=10 CenterZ=0 NormalX=0 NormalY=0 NormalZ=1 AngleXU=0 Radius=2 StartAngle=1.5708 EndAngle=4.71239
    g13: ArcOfCircle CenterX=259.333 CenterY=10 CenterZ=0 NormalX=0 NormalY=0 NormalZ=1 AngleXU=0 Radius=2 StartAngle=4.71239 EndAngle=7.85398
    g14: LineSegment StartX=249.333 StartY=8 StartZ=0 EndX=259.333 EndY=8 EndZ=0
    g15: LineSegment StartX=259.333 StartY=12 StartZ=0 EndX=249.333 EndY=12 EndZ=0
  constraints (28):
    c: Tangent(g0,g2) = -1.5708
    c: Tangent(g2,g1) = -1.5708
    c: Tangent(g1,g3) = -1.5708
    c: Tangent(g3,g0) = -1.5708
    c: Coincident(g0,g-3)
    c: Coincident(g1,g-4)
    c: Tangent(g4,g6) = -1.5708
    c: Tangent(g6,g5) = -1.5708
    c: Tangent(g5,g7) = -1.5708
    c: Tangent(g7,g4) = -1.5708
    c: Coincident(g4,g-5)
    c: Coincident(g5,g-6)
    c: Tangent(g8,g10) = -1.5708
    c: Tangent(g10,g9) = -1.5708
    c: Tangent(g9,g11) = -1.5708
    c: Tangent(g11,g8) = -1.5708
    c: Coincident(g8,g-7)
    c: Coincident(g9,g-8)
    c: Tangent(g12,g14) = -1.5708
    c: Tangent(g14,g13) = -1.5708
    c: Tangent(g13,g15) = -1.5708
    c: Tangent(g15,g12) = -1.5708
    c: Coincident(g12,g-9)
    c: Coincident(g13,g-10)
    c: Coincident(g0,g-3)
    c: Coincident(g4,g-5)
    c: Coincident(g8,g-7)
    c: Coincident(g-9,g12)
FEATURE [PartDesign::Pocket] Pocket014
  BaseFeature = -> Pad022
  Direction = (0,-1,2e-16)
  Length = 5
  Length2 = 100
  Profile = -> Sketch033
  SideType = 2
  Suppressed = false
  Type = 1
  Type2 = 0
FEATURE [Sketcher::SketchObject] Sketch034
  ArcFitTolerance = 0
  AttachmentSupport = -> [Pad020]
  ExternalTypes = [0]
  FullyConstrained = true
  MakeInternals = false
  MapMode = 5
  Placement = pos=(0,0,18) rot=(0,0,1;0rad)
  _ExternalGeoVersion = 0
  expr: Constraints[10] = <<Variables>>.SupportWasherClearanceDiammeter
  expr: Constraints[11] = <<Variables>>.SupportWasherClearanceDiammeter
  expr: Constraints[6] = <<Variables>>.SupportWasherClearanceDiammeter
  expr: Constraints[7] = <<Variables>>.SupportWasherClearanceDiammeter
  expr: Constraints[8] = <<Variables>>.SupportWasherClearanceDiammeter
  expr: Constraints[9] = <<Variables>>.SupportWasherClearanceDiammeter
  sketch-geometry (6):
    g0: Circle CenterX=0.666667 CenterY=353.333 CenterZ=0 NormalX=0 NormalY=0 NormalZ=1 AngleXU=0 Radius=8.5
    g1: Circle CenterX=0.666667 CenterY=103.333 CenterZ=0 NormalX=0 NormalY=0 NormalZ=1 AngleXU=0 Radius=8.5
    g2: Circle CenterX=0.666667 CenterY=75 CenterZ=0 NormalX=0 NormalY=0 NormalZ=1 AngleXU=0 Radius=8.5
    g3: Circle CenterX=0.666667 CenterY=-175 CenterZ=0 NormalX=0 NormalY=0 NormalZ=1 AngleXU=0 Radius=8.5
    g4: Circle CenterX=0.666667 CenterY=-203.333 CenterZ=0 NormalX=0 NormalY=0 NormalZ=1 AngleXU=0 Radius=8.5
    g5: Circle CenterX=0.666667 CenterY=-453.333 CenterZ=0 NormalX=0 NormalY=0 NormalZ=1 AngleXU=0 Radius=8.5
  constraints (12):
    c: Coincident(g0,g-3)
    c: Coincident(g1,g-4)
    c: Coincident(g2,g-5)
    c: Coincident(g3,g-6)
    c: Coincident(g4,g-7)
    c: Coincident(g5,g-8)
    c: Diameter(g0) = 17
    c: Diameter(g1) = 17
    c: Diameter(g2) = 17
    c: Diameter(g3) = 17
    c: Diameter(g4) = 17
    c: Diameter(g5) = 17
FEATURE [PartDesign::Pocket] Pocket015
  BaseFeature = -> Pad020
  Direction = (0,0,-1)
  Length = 5
  Length2 = 100
  Profile = -> Sketch034
  SideType = 2
  Suppressed = false
  Type = 1
  Type2 = 0
FEATURE [PartDesign::Body] Body020  label="VerticalSupport_Right_Body"
  AllowCompound = true
  Group = -> [Sketch029,Pad020,Sketch034,Pocket015]
  Origin = -> Origin035
  Placement = pos=(-404,50,0) rot=(0,0,1;0rad)
  Tip = -> Pocket015
  expr: .Placement.Base.x = -(<<Variables>>.OveralPadLength - <<Variables>>.SupportHeight) / 2
  expr: .Placement.Base.y = <<Variables>>.CommandWidth / 2
FEATURE [Sketcher::SketchObject] Sketch035
  ArcFitTolerance = 0
  AttachmentSupport = -> [XY_Plane025]
  ExternalTypes = [0]
  FullyConstrained = true
  MakeInternals = false
  MapMode = 5
  _ExternalGeoVersion = 0
  expr: Constraints[8] = <<Variables>>.OveralPadLength + <<Variables>>.CommandWidth
  expr: Constraints[9] = <<Variables>>.SupportHeight
  sketch-geometry (4):
    g0: LineSegment StartX=-13.5 StartY=467.5 StartZ=0 EndX=13.5 EndY=467.5 EndZ=0
    g1: LineSegment StartX=13.5 StartY=467.5 StartZ=0 EndX=13.5 EndY=-467.5 EndZ=0
    g2: LineSegment StartX=13.5 StartY=-467.5 StartZ=0 EndX=-13.5 EndY=-467.5 EndZ=0
    g3: LineSegment StartX=-13.5 StartY=-467.5 StartZ=0 EndX=-13.5 EndY=467.5 EndZ=0
  constraints (11):
    c: Coincident(g0,g1)
    c: Coincident(g1,g2)
    c: Coincident(g2,g3)
    c: Coincident(g3,g0)
    c: Horizontal(g0)
    c: Horizontal(g2)
    c: Vertical(g1)
    c: Vertical(g3)
    c: DistanceY(g3,g3) = 935
    c: DistanceX(g0,g0) = 27
    c: Symmetric(g0,g2,g-1)
FEATURE [PartDesign::Pad] Pad024
  AlongSketchNormal = false
  Direction = (0,0,1)
  Length = 18
  Length2 = 100
  Profile = -> Sketch035
  SideType = 0
  Suppressed = false
  Type = 0
  Type2 = 0
  expr: Length = <<Variables>>.SupportThickness
FEATURE [Sketcher::SketchObject] Sketch036
  ArcFitTolerance = 0
  AttachmentSupport = -> [Pad024]
  ExternalTypes = [0]
  FullyConstrained = true
  MakeInternals = false
  MapMode = 5
  Placement = pos=(0,0,18) rot=(0,0,1;0rad)
  _ExternalGeoVersion = 0
  expr: Constraints[10] = <<Variables>>.SupportWasherClearanceDiammeter
  expr: Constraints[11] = <<Variables>>.SupportWasherClearanceDiammeter
  expr: Constraints[6] = <<Variables>>.SupportWasherClearanceDiammeter
  expr: Constraints[7] = <<Variables>>.SupportWasherClearanceDiammeter
  expr: Constraints[8] = <<Variables>>.SupportWasherClearanceDiammeter
  expr: Constraints[9] = <<Variables>>.SupportWasherClearanceDiammeter
  sketch-geometry (6):
    g0: Circle CenterX=-0.666667 CenterY=353.333 CenterZ=0 NormalX=0 NormalY=0 NormalZ=1 AngleXU=0 Radius=8.5
    g1: Circle CenterX=-0.666667 CenterY=103.333 CenterZ=0 NormalX=0 NormalY=0 NormalZ=1 AngleXU=0 Radius=8.5
    g2: Circle CenterX=-0.666667 CenterY=75 CenterZ=0 NormalX=0 NormalY=0 NormalZ=1 AngleXU=0 Radius=8.5
    g3: Circle CenterX=-0.666667 CenterY=-175 CenterZ=0 NormalX=0 NormalY=0 NormalZ=1 AngleXU=0 Radius=8.5
    g4: Circle CenterX=-0.666667 CenterY=-203.333 CenterZ=0 NormalX=0 NormalY=0 NormalZ=1 AngleXU=0 Radius=8.5
    g5: Circle CenterX=-0.666667 CenterY=-453.333 CenterZ=0 NormalX=0 NormalY=0 NormalZ=1 AngleXU=0 Radius=8.5
  constraints (12):
    c: Coincident(g0,g-3)
    c: Coincident(g1,g-4)
    c: Coincident(g2,g-5)
    c: Coincident(g3,g-6)
    c: Coincident(g4,g-7)
    c: Coincident(g5,g-8)
    c: Diameter(g0) = 17
    c: Diameter(g1) = 17
    c: Diameter(g2) = 17
    c: Diameter(g3) = 17
    c: Diameter(g4) = 17
    c: Diameter(g5) = 17
FEATURE [PartDesign::Pocket] Pocket016
  BaseFeature = -> Pad024
  Direction = (0,0,-1)
  Length = 5
  Length2 = 100
  Profile = -> Sketch036
  SideType = 2
  Suppressed = false
  Type = 1
  Type2 = 0
FEATURE [PartDesign::Body] Body024  label="VerticalSupport_Left_Body"
  AllowCompound = true
  Group = -> [Sketch035,Pad024,Sketch036,Pocket016]
  Origin = -> Origin039
  Placement = pos=(404,50,0) rot=(0,0,1;0rad)
  Tip = -> Pocket016
  expr: .Placement.Base.x = (<<Variables>>.OveralPadLength - <<Variables>>.SupportHeight) / 2
  expr: .Placement.Base.y = <<Variables>>.CommandWidth / 2
FEATURE [Sketcher::SketchObject] Sketch037
  ArcFitTolerance = 0
  AttachmentSupport = -> [Pocket014]
  ExternalTypes = [0]
  FullyConstrained = true
  MakeInternals = false
  MapMode = 5
  Placement = pos=(0,0,18) rot=(0,0,1;0rad)
  _ExternalGeoVersion = 0
  expr: Constraints[4] = <<Variables>>.SupportWasherClearanceDiammeter
  expr: Constraints[5] = <<Variables>>.SupportWasherClearanceDiammeter
  expr: Constraints[6] = <<Variables>>.SupportWasherClearanceDiammeter
  expr: Constraints[7] = <<Variables>>.SupportWasherClearanceDiammeter
  sketch-geometry (4):
    g0: Circle CenterX=-153.333 CenterY=-0.666667 CenterZ=0 NormalX=0 NormalY=0 NormalZ=1 AngleXU=0 Radius=8.5
    g1: Circle CenterX=-125 CenterY=-0.666667 CenterZ=0 NormalX=0 NormalY=0 NormalZ=1 AngleXU=0 Radius=8.5
    g2: Circle CenterX=125 CenterY=-0.666667 CenterZ=0 NormalX=0 NormalY=0 NormalZ=1 AngleXU=0 Radius=8.5
    g3: Circle CenterX=153.333 CenterY=-0.666667 CenterZ=0 NormalX=0 NormalY=0 NormalZ=1 AngleXU=0 Radius=8.5
  constraints (8):
    c: Coincident(g0,g-3)
    c: Coincident(g1,g-4)
    c: Coincident(g2,g-5)
    c: Coincident(g3,g-6)
    c: Diameter(g0) = 17
    c: Diameter(g1) = 17
    c: Diameter(g2) = 17
    c: Diameter(g3) = 17
FEATURE [PartDesign::Pocket] Pocket017
  BaseFeature = -> Pocket014
  Direction = (0,0,-1)
  Length = 5
  Length2 = 100
  Profile = -> Sketch037
  SideType = 2
  Suppressed = false
  Type = 1
  Type2 = 0
FEATURE [PartDesign::Body] Body022  label="HorizontalSupport_Up_Body"
  AllowCompound = true
  Group = -> [Sketch031,Pad022,Sketch033,Pocket014,Sketch037,Pocket017]
  Origin = -> Origin037
  Placement = pos=(0,404,0) rot=(0,0,1;0rad)
  Tip = -> Pocket017
  expr: .Placement.Base.y = (<<Variables>>.OveralPadLength - <<Variables>>.SupportHeight) / 2
FEATURE [Sketcher::SketchObject] Sketch038
  ArcFitTolerance = 0
  AttachmentSupport = -> [Pad021]
  ExternalTypes = [0]
  FullyConstrained = true
  MakeInternals = false
  MapMode = 5
  Placement = pos=(0,0,18) rot=(0,0,1;0rad)
  _ExternalGeoVersion = 0
  expr: Constraints[4] = <<Variables>>.SupportWasherClearanceDiammeter
  expr: Constraints[5] = <<Variables>>.SupportWasherClearanceDiammeter
  expr: Constraints[6] = <<Variables>>.SupportWasherClearanceDiammeter
  expr: Constraints[7] = <<Variables>>.SupportWasherClearanceDiammeter
  sketch-geometry (4):
    g0: Circle CenterX=-153.333 CenterY=0.666667 CenterZ=0 NormalX=0 NormalY=0 NormalZ=1 AngleXU=0 Radius=8.5
    g1: Circle CenterX=-125 CenterY=0.666667 CenterZ=0 NormalX=0 NormalY=0 NormalZ=1 AngleXU=0 Radius=8.5
    g2: Circle CenterX=125 CenterY=0.666667 CenterZ=0 NormalX=0 NormalY=0 NormalZ=1 AngleXU=0 Radius=8.5
    g3: Circle CenterX=153.333 CenterY=0.666667 CenterZ=0 NormalX=0 NormalY=0 NormalZ=1 AngleXU=0 Radius=8.5
  constraints (8):
    c: Coincident(g0,g-3)
    c: Coincident(g1,g-4)
    c: Coincident(g2,g-6)
    c: Coincident(g3,g-5)
    c: Diameter(g0) = 17
    c: Diameter(g1) = 17
    c: Diameter(g2) = 17
    c: Diameter(g3) = 17
FEATURE [PartDesign::Pocket] Pocket018
  BaseFeature = -> Pad021
  Direction = (0,0,-1)
  Length = 5
  Length2 = 100
  Profile = -> Sketch038
  SideType = 2
  Suppressed = false
  Type = 1
  Type2 = 0
FEATURE [PartDesign::Body] Body021  label="HorizontalSupport_Bottom_Body"
  AllowCompound = true
  Group = -> [Sketch030,Pad021,Sketch038,Pocket018]
  Origin = -> Origin036
  Placement = pos=(0,-404,0) rot=(0,0,1;0rad)
  Tip = -> Pocket018
  expr: .Placement.Base.y = -(<<Variables>>.OveralPadLength - <<Variables>>.SupportHeight) / 2
FEATURE [Sketcher::SketchObject] Sketch039
  ArcFitTolerance = 0
  AttachmentSupport = -> [XY_Plane026]
  ExternalTypes = [0]
  FullyConstrained = true
  MakeInternals = false
  MapMode = 5
  _ExternalGeoVersion = 0
  expr: Constraints[8] = <<Variables>>.OveralPadLength / 3 - <<Variables>>.SupportHeight
  expr: Constraints[9] = <<Variables>>.SupportHeight
  sketch-geometry (4):
    g0: LineSegment StartX=-125.667 StartY=13.5 StartZ=0 EndX=125.667 EndY=13.5 EndZ=0
    g1: LineSegment StartX=125.667 StartY=13.5 StartZ=0 EndX=125.667 EndY=-13.5 EndZ=0
    g2: LineSegment StartX=125.667 StartY=-13.5 StartZ=0 EndX=-125.667 EndY=-13.5 EndZ=0
    g3: LineSegment StartX=-125.667 StartY=-13.5 StartZ=0 EndX=-125.667 EndY=13.5 EndZ=0
  constraints (11):
    c: Coincident(g0,g1)
    c: Coincident(g1,g2)
    c: Coincident(g2,g3)
    c: Coincident(g3,g0)
    c: Horizontal(g0)
    c: Horizontal(g2)
    c: Vertical(g1)
    c: Vertical(g3)
    c: DistanceX(g0,g0) = 251.333
    c: DistanceY(g1,g1) = 27
    c: Symmetric(g0,g1,g-1)
FEATURE [PartDesign::Pad] Pad025
  AlongSketchNormal = false
  Direction = (0,0,1)
  Length = 18
  Length2 = 100
  Profile = -> Sketch039
  SideType = 0
  Suppressed = false
  Type = 0
  Type2 = 0
  expr: Length = <<Variables>>.SupportThickness
FEATURE [Sketcher::SketchObject] Sketch040
  ArcFitTolerance = 0
  AttachmentSupport = -> [Pad025]
  ExternalTypes = [0]
  FullyConstrained = true
  MakeInternals = false
  MapMode = 5
  Placement = pos=(0,13.5,0) rot=(0,0.707107,0.707107;3.14159rad)
  _ExternalGeoVersion = 0
  sketch-geometry (8):
    g0: ArcOfCircle CenterX=-120 CenterY=10 CenterZ=0 NormalX=0 NormalY=0 NormalZ=1 AngleXU=0 Radius=2 StartAngle=1.5708 EndAngle=4.71239
    g1: ArcOfCircle CenterX=-110 CenterY=10 CenterZ=0 NormalX=0 NormalY=0 NormalZ=1 AngleXU=0 Radius=2 StartAngle=4.71239 EndAngle=7.85398
    g2: LineSegment StartX=-120 StartY=8 StartZ=0 EndX=-110 EndY=8 EndZ=0
    g3: LineSegment StartX=-110 StartY=12 StartZ=0 EndX=-120 EndY=12 EndZ=0
    g4: ArcOfCircle CenterX=110 CenterY=10 CenterZ=0 NormalX=0 NormalY=0 NormalZ=1 AngleXU=0 Radius=2 StartAngle=1.5708 EndAngle=4.71239
    g5: ArcOfCircle CenterX=120 CenterY=10 CenterZ=0 NormalX=0 NormalY=0 NormalZ=1 AngleXU=0 Radius=2 StartAngle=4.71239 EndAngle=7.85398
    g6: LineSegment StartX=110 StartY=8 StartZ=0 EndX=120 EndY=8 EndZ=0
    g7: LineSegment StartX=120 StartY=12 StartZ=0 EndX=110 EndY=12 EndZ=0
  constraints (19):
    c: Tangent(g0,g2) = -1.5708
    c: Tangent(g2,g1) = -1.5708
    c: Tangent(g1,g3) = -1.5708
    c: Tangent(g3,g0) = -1.5708
    c: Equal(g0,g1)
    c: Tangent(g4,g6) = -1.5708
    c: Tangent(g6,g5) = -1.5708
    c: Tangent(g5,g7) = -1.5708
    c: Tangent(g7,g4) = -1.5708
    c: Equal(g4,g5)
    c: Horizontal(g3)
    c: Horizontal(g7)
    c: DistanceX(g0,g1) = 10
    c: DistanceX(g4,g5) = 10
    c: Diameter(g1) = 4
    c: Diameter(g5) = 4
    c: Symmetric(g1,g4,g-2)
    c: DistanceY(g-1,g1) = 10
    c: DistanceX(g1,g-1) = 110
FEATURE [PartDesign::Pocket] Pocket019
  BaseFeature = -> Pad025
  Direction = (0,-1,2e-16)
  Length = 5
  Length2 = 100
  Profile = -> Sketch040
  SideType = 2
  Suppressed = false
  Type = 1
  Type2 = 0
FEATURE [PartDesign::LinearPattern] LinearPattern007
  BaseFeature = -> Pocket019
  Direction = -> Y_Axis026
  Length = 556.667
  Length2 = 100
  Mode = 0
  Mode2 = 0
  Occurrences = 3
  Occurrences2 = 1
  Offset = 278.333
  Offset2 = 10
  Originals = -> [Pocket019,Pad025]
  Reversed = true
  Reversed2 = false
  SpacingPattern = [0]
  SpacingPattern2 = [0]
  Spacings = [-1,-1]
  Suppressed = false
  TransformMode = 0
  expr: Length = <<Variables>>.OveralPadLength / 3 * 2
FEATURE [PartDesign::Body] Body025  label="HorizontalCrossing_Left_Body"
  AllowCompound = true
  Group = -> [Sketch039,Pad025,Sketch040,Pocket019,LinearPattern007]
  Origin = -> Origin040
  Placement = pos=(-139.333,278.333,0) rot=(0,0,1;0rad)
  Tip = -> LinearPattern007
  expr: .Placement.Base.x = -<<Variables>>.OveralPadLength / 3 + <<Variables>>.PadLength / 2
  expr: .Placement.Base.y = <<Variables>>.OveralPadLength / 3
FEATURE [Sketcher::SketchObject] Sketch041
  ArcFitTolerance = 0
  AttachmentSupport = -> [XY_Plane027]
  ExternalTypes = [0]
  FullyConstrained = true
  MakeInternals = false
  MapMode = 5
  _ExternalGeoVersion = 0
  expr: Constraints[8] = <<Variables>>.OveralPadLength / 3 - <<Variables>>.SupportHeight
  expr: Constraints[9] = <<Variables>>.SupportHeight
  sketch-geometry (4):
    g0: LineSegment StartX=-125.667 StartY=13.5 StartZ=0 EndX=125.667 EndY=13.5 EndZ=0
    g1: LineSegment StartX=125.667 StartY=13.5 StartZ=0 EndX=125.667 EndY=-13.5 EndZ=0
    g2: LineSegment StartX=125.667 StartY=-13.5 StartZ=0 EndX=-125.667 EndY=-13.5 EndZ=0
    g3: LineSegment StartX=-125.667 StartY=-13.5 StartZ=0 EndX=-125.667 EndY=13.5 EndZ=0
  constraints (11):
    c: Coincident(g0,g1)
    c: Coincident(g1,g2)
    c: Coincident(g2,g3)
    c: Coincident(g3,g0)
    c: Horizontal(g0)
    c: Horizontal(g2)
    c: Vertical(g1)
    c: Vertical(g3)
    c: DistanceX(g0,g0) = 251.333
    c: DistanceY(g1,g1) = 27
    c: Symmetric(g0,g1,g-1)
FEATURE [PartDesign::Pad] Pad026
  AlongSketchNormal = false
  Direction = (0,0,1)
  Length = 18
  Length2 = 100
  Profile = -> Sketch041
  SideType = 0
  Suppressed = false
  Type = 0
  Type2 = 0
  expr: Length = <<Variables>>.SupportThickness
FEATURE [Sketcher::SketchObject] Sketch042
  ArcFitTolerance = 0
  AttachmentSupport = -> [Pad026]
  ExternalTypes = [0]
  FullyConstrained = true
  MakeInternals = false
  MapMode = 5
  Placement = pos=(0,13.5,0) rot=(0,0.707107,0.707107;3.14159rad)
  _ExternalGeoVersion = 0
  sketch-geometry (8):
    g0: ArcOfCircle CenterX=-120 CenterY=10 CenterZ=0 NormalX=0 NormalY=0 NormalZ=1 AngleXU=0 Radius=2 StartAngle=1.5708 EndAngle=4.71239
    g1: ArcOfCircle CenterX=-110 CenterY=10 CenterZ=0 NormalX=0 NormalY=0 NormalZ=1 AngleXU=0 Radius=2 StartAngle=4.71239 EndAngle=7.85398
    g2: LineSegment StartX=-120 StartY=8 StartZ=0 EndX=-110 EndY=8 EndZ=0
    g3: LineSegment StartX=-110 StartY=12 StartZ=0 EndX=-120 EndY=12 EndZ=0
    g4: ArcOfCircle CenterX=110 CenterY=10 CenterZ=0 NormalX=0 NormalY=0 NormalZ=1 AngleXU=0 Radius=2 StartAngle=1.5708 EndAngle=4.71239
    g5: ArcOfCircle CenterX=120 CenterY=10 CenterZ=0 NormalX=0 NormalY=0 NormalZ=1 AngleXU=0 Radius=2 StartAngle=4.71239 EndAngle=7.85398
    g6: LineSegment StartX=110 StartY=8 StartZ=0 EndX=120 EndY=8 EndZ=0
    g7: LineSegment StartX=120 StartY=12 StartZ=0 EndX=110 EndY=12 EndZ=0
  constraints (19):
    c: Tangent(g0,g2) = -1.5708
    c: Tangent(g2,g1) = -1.5708
    c: Tangent(g1,g3) = -1.5708
    c: Tangent(g3,g0) = -1.5708
    c: Equal(g0,g1)
    c: Tangent(g4,g6) = -1.5708
    c: Tangent(g6,g5) = -1.5708
    c: Tangent(g5,g7) = -1.5708
    c: Tangent(g7,g4) = -1.5708
    c: Equal(g4,g5)
    c: Horizontal(g3)
    c: Horizontal(g7)
    c: Symmetric(g1,g4,g-2)
    c: Diameter(g1) = 4
    c: Diameter(g5) = 4
    c: DistanceX(g0,g1) = 10
    c: DistanceX(g4,g5) = 10
    c: DistanceY(g-1,g1) = 10
    c: DistanceX(g1,g-1) = 110
FEATURE [PartDesign::Pocket] Pocket020
  BaseFeature = -> Pad026
  Direction = (0,-1,2e-16)
  Length = 5
  Length2 = 100
  Profile = -> Sketch042
  SideType = 2
  Suppressed = false
  Type = 1
  Type2 = 0
FEATURE [PartDesign::LinearPattern] LinearPattern008
  BaseFeature = -> Pocket020
  Direction = -> Y_Axis027
  Length = 556.667
  Length2 = 100
  Mode = 0
  Mode2 = 0
  Occurrences = 3
  Occurrences2 = 1
  Offset = 278.333
  Offset2 = 10
  Originals = -> [Pocket020,Pad026]
  Reversed = true
  Reversed2 = false
  SpacingPattern = [0]
  SpacingPattern2 = [0]
  Spacings = [-1,-1]
  Suppressed = false
  TransformMode = 0
  expr: Length = <<Variables>>.OveralPadLength / 3 * 2
FEATURE [PartDesign::Body] Body026  label="HorizontalCrossing_Right_Body"
  AllowCompound = true
  Group = -> [Sketch041,Pad026,Sketch042,Pocket020,LinearPattern008]
  Origin = -> Origin041
  Placement = pos=(139.333,278.333,0) rot=(0,0,1;0rad)
  Tip = -> LinearPattern008
  expr: .Placement.Base.x = <<Variables>>.OveralPadLength / 3 - <<Variables>>.PadLength / 2
  expr: .Placement.Base.y = <<Variables>>.OveralPadLength / 3
PROVENANCE & LICENSES
A FreeCAD (.FCStd) document from a public repository crawl; recipes are the document's own serialized feature recipes (and, for linked parts, companion documents' recipes).
License: mit.
